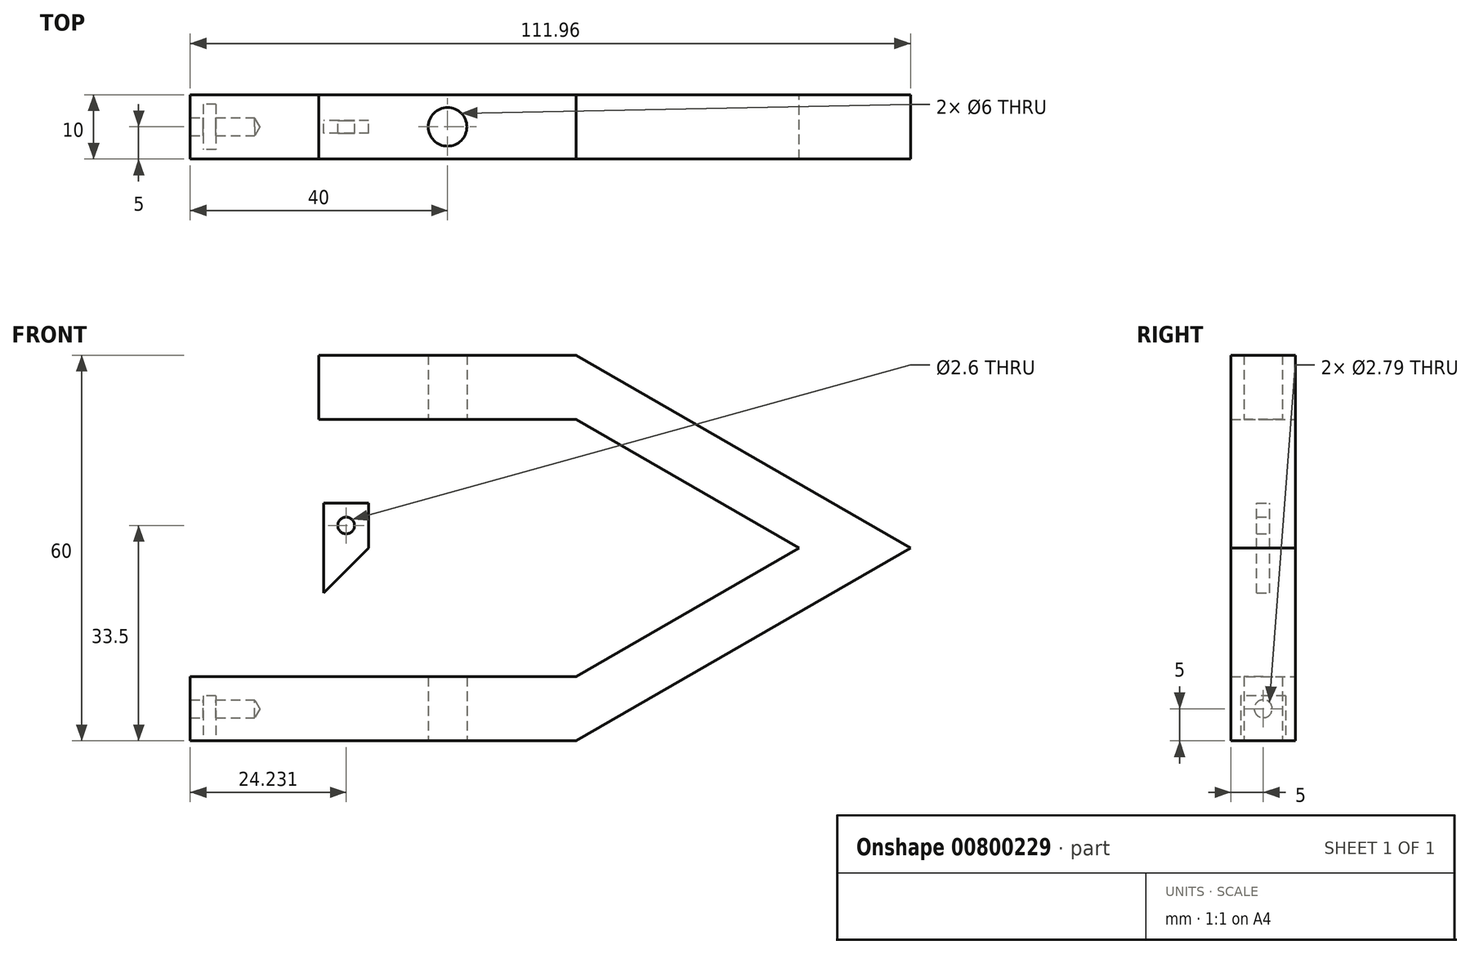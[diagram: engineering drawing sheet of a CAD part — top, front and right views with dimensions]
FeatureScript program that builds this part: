
annotation { "Feature Type Name" : "Feature", "Feature Type Description" : "" }
export const myFeature = defineFeature(function(context is Context, id is Id, definition is map)
    precondition{}
    {
        {
            var Q0;
            Q0=qCreatedBy(makeId("Front.planeOp"),FACE);
            var sketch = newSketch(context, id + "F0", { "sketchPlane" : qUnion([Q0])});
            skLineSegment(sketch, "E0", {"start": v(-40, 30) * mm, "end": v(0, 30) * mm});
            skLineSegment(sketch, "E1", {"start": v(0, 30) * mm, "end": v(51.96, 0) * mm});
            skLineSegment(sketch, "E2", {"start": v(51.96, 0) * mm, "end": v(0, -30) * mm});
            skLineSegment(sketch, "E3", {"start": v(0, -30) * mm, "end": v(-60, -30) * mm});
            skLineSegment(sketch, "E4", {"start": v(-60, -20) * mm, "end": v(0, -20) * mm});
            skLineSegment(sketch, "E5", {"start": v(0, -20) * mm, "end": v(34.64, 0) * mm});
            skLineSegment(sketch, "E6", {"start": v(34.64, 0) * mm, "end": v(0, 20) * mm});
            skLineSegment(sketch, "E7", {"start": v(0, 20) * mm, "end": v(-40, 20) * mm});
            skLineSegment(sketch, "E8", {"start": v(-40, 20) * mm, "end": v(-40, 30) * mm});
            skLineSegment(sketch, "E9", {"start": v(0, 20) * mm, "end": v(0, -20) * mm, "construction": true});
            skPoint(sketch, "E10", {"position": v(0, 0) * mm});
            skLineSegment(sketch, "E11", {"start": v(-60, -20) * mm, "end": v(-60, -30) * mm});
            skSolve(sketch);
        }
        {
            var Q0;
            Q0=makeQuery(id+"F0.imprint","IMPRINT",FACE,{"disambiguationData":[TD([[makeQuery(id+"F0.imprint","IMPRINT",EDGE,{"derivedFrom":sQuery(id+"F0.wireOp",EDGE,"E0")}),-1.0]])]});
            extrude(context, id + "F1", {"entities" : qUnion([Q0]), "depth" : 10 * mm, "offsetDistance" : 25 * mm, "symmetric" : true});
        }
        {
            var Q0;
            Q0=makeQuery(id+"F1.opExtrude","SWEPT_FACE",FACE,{"disambiguationData":[OSD([sQuery(id+"F0.wireOp",EDGE,"E3")])]});
            var sketch = newSketch(context, id + "F2", { "sketchPlane" : qUnion([Q0])});
            skLineSegment(sketch, "E12.bottom", {"start": v(-56, -3.5) * mm, "end": v(-58, -3.5) * mm});
            skLineSegment(sketch, "E12.top", {"start": v(-56, 3.5) * mm, "end": v(-58, 3.5) * mm});
            skLineSegment(sketch, "E12.left", {"start": v(-56, -3.5) * mm, "end": v(-56, 3.5) * mm});
            skLineSegment(sketch, "E12.right", {"start": v(-58, -3.5) * mm, "end": v(-58, 3.5) * mm});
            skSolve(sketch);
        }
        {
            var Q0;
            Q0=makeQuery(id+"F2.imprint","IMPRINT",FACE,{"disambiguationData":[TD([[makeQuery(id+"F2.imprint","IMPRINT",EDGE,{"derivedFrom":sQuery(id+"F2.wireOp",EDGE,"E12.bottom")}),-1.0]])]});
            extrude(context, id + "F3", {"entities" : qUnion([Q0]), "operationType" : NewBodyOperationType.REMOVE, "oppositeDirection" : true, "depth" : 7 * mm, "offsetDistance" : 25 * mm});
        }
        {
            var Q0;
            Q0=makeQuery(id+"F1.opExtrude","SWEPT_FACE",FACE,{"disambiguationData":[OSD([sQuery(id+"F0.wireOp",EDGE,"E11")])]});
            var sketch = newSketch(context, id + "F4", { "sketchPlane" : qUnion([Q0])});
            skLineSegment(sketch, "E13", {"start": v(-5, -20) * mm, "end": v(5, -30) * mm, "construction": true});
            skPoint(sketch, "E14", {"position": v(0, -25) * mm});
            skSolve(sketch);
        }
        {
            var Q0;
            Q0=sQuery(id+"F4.wireOp",VERTEX,"E14");
            var Q1;
            Q1=makeQuery(id+"F1.opExtrude","SWEPT_BODY",BODY,{"disambiguationData":[OSD([sQuery(id+"F0.wireOp",EDGE,"E0"),sQuery(id+"F0.wireOp",EDGE,"E1"),sQuery(id+"F0.wireOp",EDGE,"E2"),sQuery(id+"F0.wireOp",EDGE,"E3"),sQuery(id+"F0.wireOp",EDGE,"E4"),sQuery(id+"F0.wireOp",EDGE,"E5"),sQuery(id+"F0.wireOp",EDGE,"E6"),sQuery(id+"F0.wireOp",EDGE,"E7"),sQuery(id+"F0.wireOp",EDGE,"E8"),sQuery(id+"F0.wireOp",EDGE,"E11")])]});
            hole(context, id + "F5", {"style" : HoleStyle.SIMPLE, "endStyle" : HoleEndStyle.BLIND, "standardTappedOrClearance" : lookupTablePath({ "standard" : "ANSI", "fit" : "Normal (ASME)", "size" : "#3", "type" : "Clearance" }), "standardBlindInLast" : lookupTablePath({ "fit" : "Free", "standard" : "ANSI", "size" : "#3", "type" : "Clearance" }), "holeDiameter" : 2.8 * mm, "majorDiameter" : 5 * mm, "holeDepth" : 10 * mm, "isTappedThrough" : true, "tappedDepth" : 12 * mm, "tapClearance" : 3, "locations" : qUnion([Q0]), "scope" : qUnion([Q1]), "startStyle" : HoleStartStyle.PART});
        }
        {
            var Q0;
            Q0=makeQuery(id+"F1.opExtrude","SWEPT_FACE",FACE,{"disambiguationData":[OSD([sQuery(id+"F0.wireOp",EDGE,"E0")])]});
            var sketch = newSketch(context, id + "F6", { "sketchPlane" : qUnion([Q0])});
            skLineSegment(sketch, "E15", {"start": v(-40, 5) * mm, "end": v(0, -5) * mm, "construction": true});
            skPoint(sketch, "E16", {"position": v(-20, 0) * mm});
            skSolve(sketch);
        }
        {
            var Q0;
            Q0=sQuery(id+"F6.wireOp",VERTEX,"E16");
            var Q1;
            Q1=makeQuery(id+"F1.opExtrude","SWEPT_BODY",BODY,{"disambiguationData":[OSD([sQuery(id+"F0.wireOp",EDGE,"E0"),sQuery(id+"F0.wireOp",EDGE,"E1"),sQuery(id+"F0.wireOp",EDGE,"E2"),sQuery(id+"F0.wireOp",EDGE,"E3"),sQuery(id+"F0.wireOp",EDGE,"E4"),sQuery(id+"F0.wireOp",EDGE,"E5"),sQuery(id+"F0.wireOp",EDGE,"E6"),sQuery(id+"F0.wireOp",EDGE,"E7"),sQuery(id+"F0.wireOp",EDGE,"E8"),sQuery(id+"F0.wireOp",EDGE,"NjeTLYMz-Eup0-CHey-zUee-MBfSLKDRedQZ"),sQuery(id+"F0.wireOp",EDGE,"omkWUNpl-Jj79-dlMt-0UN2-k4OaXAe8HTQ1"),sQuery(id+"F0.wireOp",EDGE,"s1lgzxZ7-UtRO-Ncqg-kDx1-q5F3pCsxJUwp")])]});
            hole(context, id + "F7", {"style" : HoleStyle.SIMPLE, "endStyle" : HoleEndStyle.THROUGH, "holeDiameter" : 6 * mm, "majorDiameter" : 5 * mm, "isTappedThrough" : true, "tappedDepth" : 12 * mm, "tapClearance" : 3, "locations" : qUnion([Q0]), "scope" : qUnion([Q1]), "startStyle" : HoleStartStyle.PART});
        }
        {
            var Q0;
            Q0=qCreatedBy(makeId("Front.planeOp"),FACE);
            var sketch = newSketch(context, id + "F8", { "sketchPlane" : qUnion([Q0])});
            skLineSegment(sketch, "E17.top", {"start": v(-32.27, 7) * mm, "end": v(-39.27, 7) * mm});
            skLineSegment(sketch, "E17.left", {"start": v(-32.27, 0) * mm, "end": v(-32.27, 7) * mm});
            skLineSegment(sketch, "E17.right", {"start": v(-39.27, 0) * mm, "end": v(-39.27, 7) * mm});
            skPoint(sketch, "E17.middle", {"position": v(-35.77, 3.5) * mm});
            skLineSegment(sketch, "E18", {"start": v(-39.27, 0) * mm, "end": v(-39.27, -7) * mm});
            skLineSegment(sketch, "E19", {"start": v(-39.27, -7) * mm, "end": v(-32.27, 0) * mm});
            skCircle(sketch, "E20", {"center": v(-35.77, 3.5) * mm, "radius": 1.3 * mm});
            skSolve(sketch);
        }
        {
            var Q0;
            Q0=makeQuery(id+"F8.imprint","IMPRINT",FACE,{"disambiguationData":[TD([[makeQuery(id+"F8.imprint","IMPRINT",EDGE,{"derivedFrom":sQuery(id+"F8.wireOp",EDGE,"E17.top")}),1.0]])]});
            extrude(context, id + "F9", {"entities" : qUnion([Q0]), "depth" : 2 * mm, "offsetDistance" : 25 * mm, "symmetric" : true});
        }
    });
